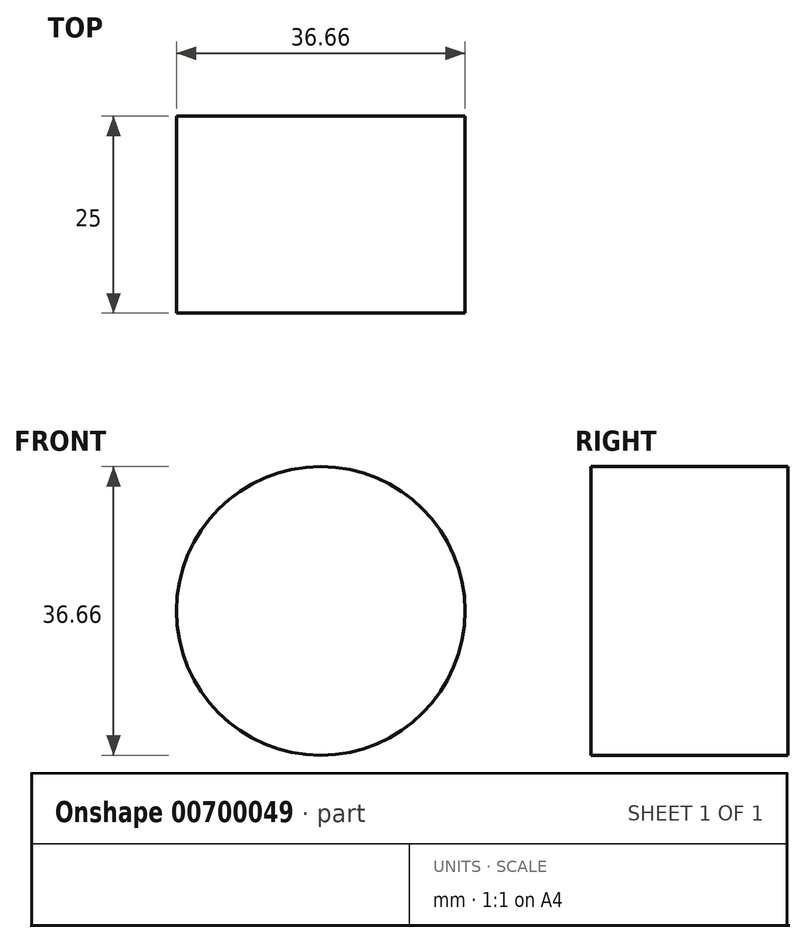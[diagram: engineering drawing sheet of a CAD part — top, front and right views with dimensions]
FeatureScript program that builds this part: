
annotation { "Feature Type Name" : "Feature", "Feature Type Description" : "" }
export const myFeature = defineFeature(function(context is Context, id is Id, definition is map)
    precondition{}
    {
        {
            var Q0;
            Q0=qCreatedBy(makeId("Front.planeOp"),FACE);
            var sketch = newSketch(context, id + "F0", { "sketchPlane" : qUnion([Q0])});
            skCircle(sketch, "E0", {"center": v(0, 0) * mm, "radius": 13.39 * mm});
            skCircle(sketch, "E1", {"center": v(12.1, 5.74) * mm, "radius": 19.42 * mm});
            skCircle(sketch, "E2", {"center": v(26.54, -7.24) * mm, "radius": 18.33 * mm});
            skSolve(sketch);
        }
        {
            var Q0;
            Q0=sQuery(id+"F0.wireOp",EDGE,"E2");
            extrude(context, id + "F1", {"bodyType" : ToolBodyType.SURFACE, "surfaceEntities" : qUnion([Q0]), "depth" : 25 * mm, "offsetDistance" : 25 * mm});
        }
    });
